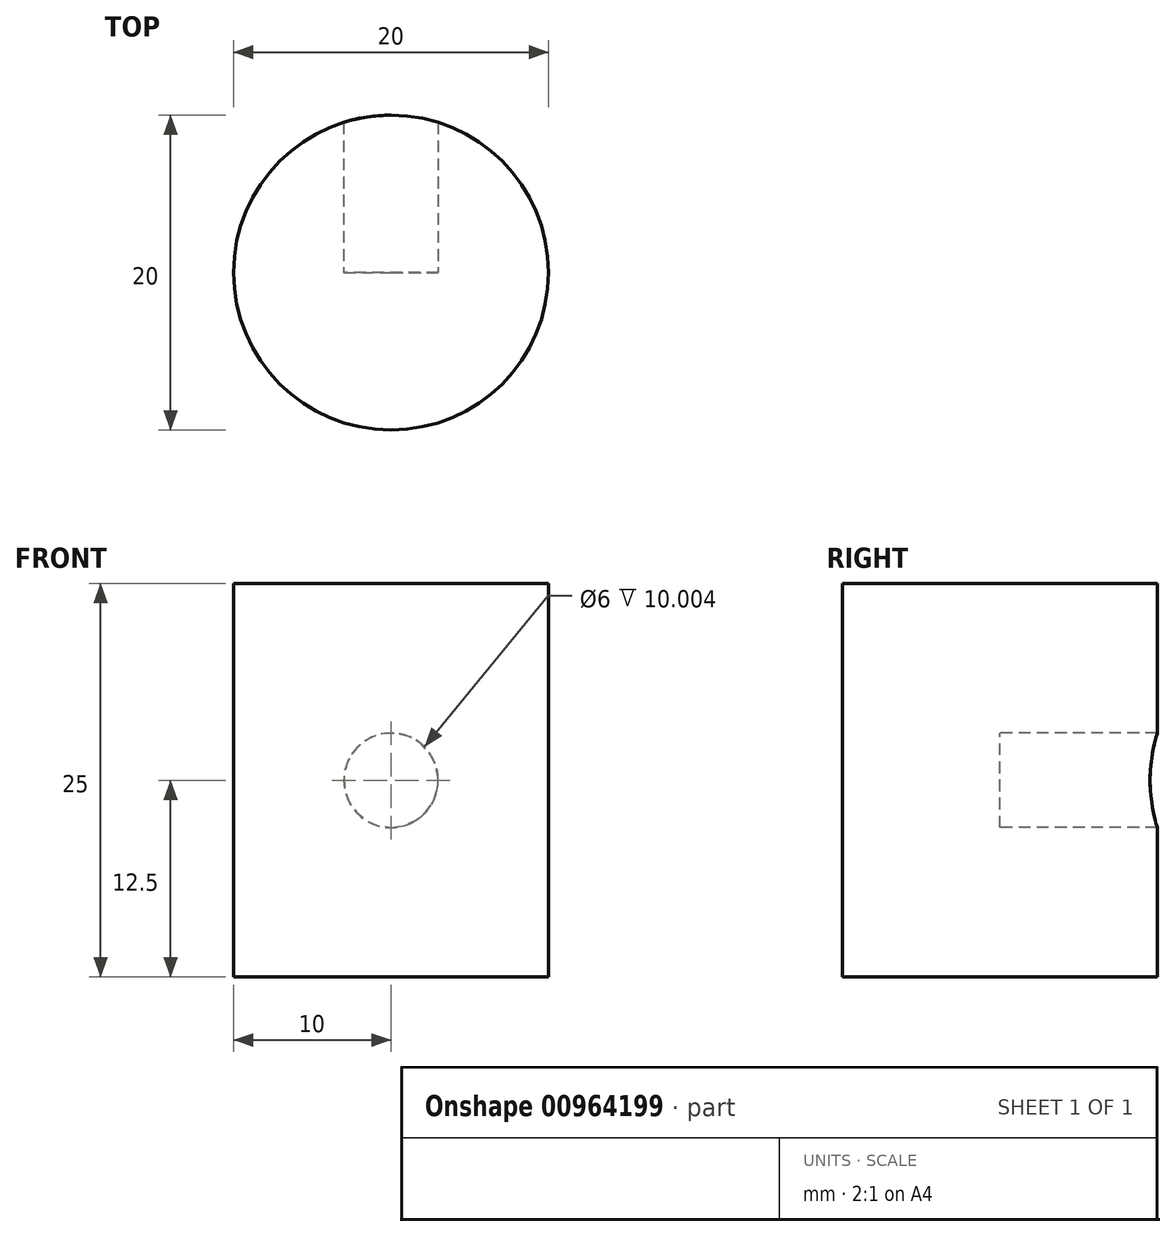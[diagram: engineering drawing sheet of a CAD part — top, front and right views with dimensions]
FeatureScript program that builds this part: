
annotation { "Feature Type Name" : "Feature", "Feature Type Description" : "" }
export const myFeature = defineFeature(function(context is Context, id is Id, definition is map)
    precondition{}
    {
        {
            var Q0;
            Q0=qCreatedBy(makeId("Top.planeOp"),FACE);
            var sketch = newSketch(context, id + "F0", { "sketchPlane" : qUnion([Q0])});
            skCircle(sketch, "E0", {"center": v(0, 0) * mm, "radius": 10 * mm});
            skSolve(sketch);
        }
        {
            var Q0;
            Q0=makeQuery(id+"F0.imprint","IMPRINT",FACE,{"disambiguationData":[TD([[makeQuery(id+"F0.imprint","IMPRINT",EDGE,{"derivedFrom":sQuery(id+"F0.wireOp",EDGE,"E0")}),1.0]])]});
            var Q1;
            Q1=sQuery(id+"F0.wireOp",EDGE,"E0");
            extrude(context, id + "F1", {"entities" : qUnion([Q0]), "surfaceEntities" : qUnion([Q1]), "depth" : 25 * mm, "offsetDistance" : 25 * mm});
        }
        {
            var Q0;
            Q0=qCreatedBy(makeId("Front.planeOp"),FACE);
            var sketch = newSketch(context, id + "F2", { "sketchPlane" : qUnion([Q0])});
            skCircle(sketch, "E1", {"center": v(0, 12.5) * mm, "radius": 3 * mm});
            skSolve(sketch);
        }
        {
            var Q0;
            Q0 = qSketchRegion(id + "F2", true);
            extrude(context, id + "F3", {"entities" : qUnion([Q0]), "operationType" : NewBodyOperationType.REMOVE, "oppositeDirection" : true, "depth" : 25 * mm, "offsetDistance" : 25 * mm});
        }
    });
